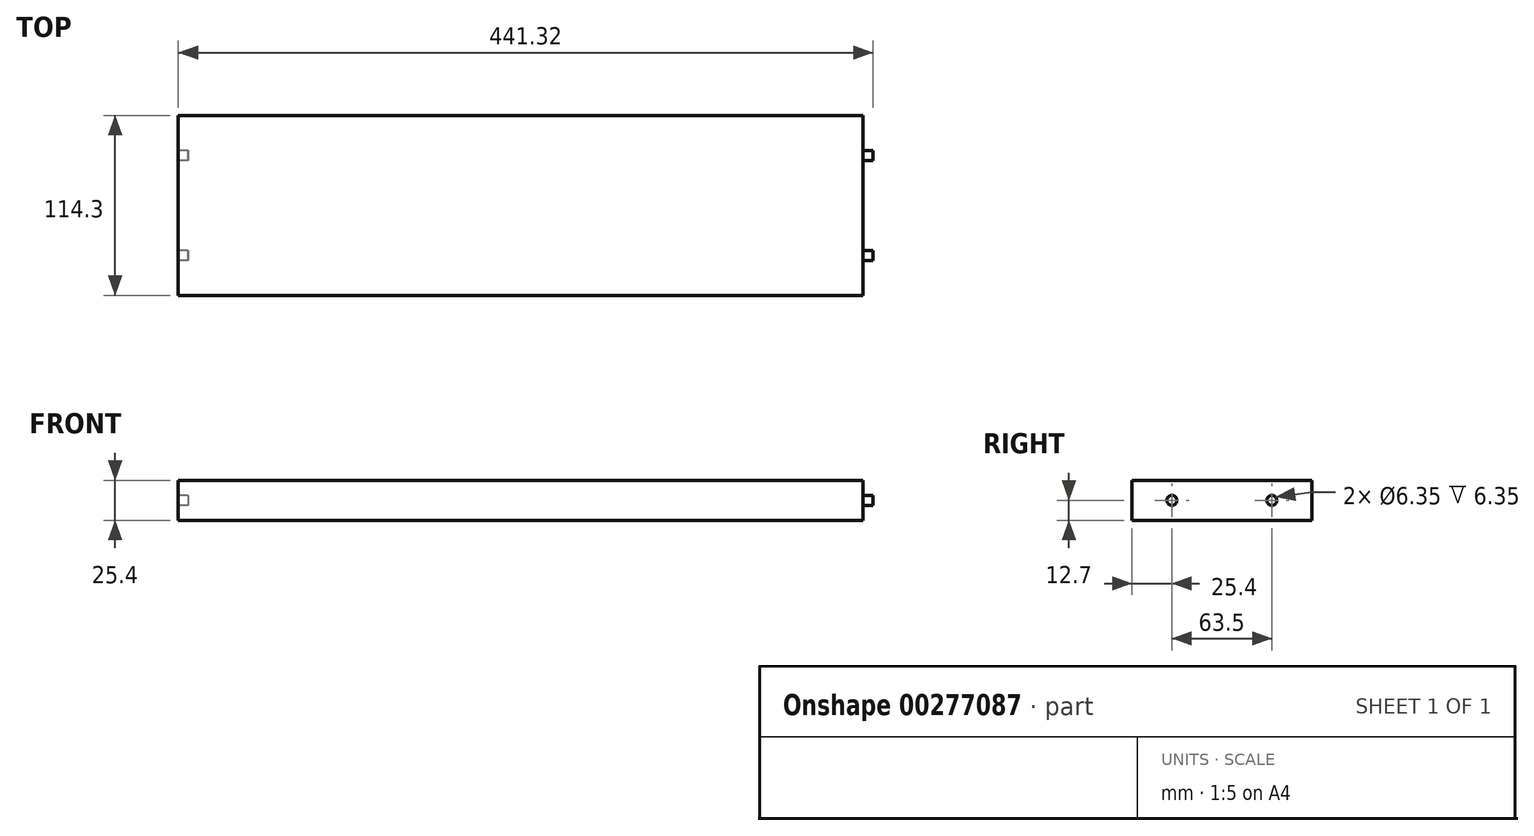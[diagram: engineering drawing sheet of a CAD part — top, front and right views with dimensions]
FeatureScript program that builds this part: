
annotation { "Feature Type Name" : "Feature", "Feature Type Description" : "" }
export const myFeature = defineFeature(function(context is Context, id is Id, definition is map)
    precondition{}
    {
        {
            var Q0;
            Q0=qCreatedBy(makeId("Front.planeOp"),FACE);
            var sketch = newSketch(context, id + "F0", { "sketchPlane" : qUnion([Q0])});
            skLineSegment(sketch, "E0.bottom", {"start": v(-71.67, 0) * mm, "end": v(369.65, 0) * mm});
            skLineSegment(sketch, "E0.top", {"start": v(-71.67, 25.4) * mm, "end": v(369.65, 25.4) * mm});
            skLineSegment(sketch, "E0.left", {"start": v(-71.67, 0) * mm, "end": v(-71.67, 25.4) * mm});
            skLineSegment(sketch, "E0.right", {"start": v(369.65, 0) * mm, "end": v(369.65, 25.4) * mm});
            skSolve(sketch);
        }
        {
            var Q0;
            Q0=makeQuery(id+"F0.imprint","IMPRINT",FACE,{"disambiguationData":[TD([[makeQuery(id+"F0.imprint","IMPRINT",EDGE,{"derivedFrom":sQuery(id+"F0.wireOp",EDGE,"E0.bottom")}),1.0]])]});
            extrude(context, id + "F1", {"entities" : qUnion([Q0]), "depth" : 114.3 * mm});
        }
        {
            var Q0;
            Q0=makeQuery(id+"F1.opExtrude","SWEPT_FACE",FACE,{"disambiguationData":[OSD([sQuery(id+"F0.wireOp",EDGE,"E0.left")])]});
            var sketch = newSketch(context, id + "F2", { "sketchPlane" : qUnion([Q0])});
            skCircle(sketch, "E1", {"center": v(25.4, 12.7) * mm, "radius": 3.18 * mm});
            skPoint(sketch, "E1.centerSnap0", {"position": v(0, 12.7) * mm});
            skCircle(sketch, "E2", {"center": v(88.9, 12.7) * mm, "radius": 3.18 * mm});
            skPoint(sketch, "E2.centerSnap0", {"position": v(114.3, 12.7) * mm});
            skSolve(sketch);
        }
        {
            var Q0;
            Q0=makeQuery(id+"F1.opExtrude","SWEPT_FACE",FACE,{"disambiguationData":[OSD([sQuery(id+"F0.wireOp",EDGE,"E0.right")])]});
            var sketch = newSketch(context, id + "F3", { "sketchPlane" : qUnion([Q0])});
            skCircle(sketch, "E3.0", {"center": v(-88.9, 12.7) * mm, "radius": 3.18 * mm});
            skCircle(sketch, "E4.0", {"center": v(-25.4, 12.7) * mm, "radius": 3.18 * mm});
            skSolve(sketch);
        }
        {
            var Q0;
            Q0=makeQuery(id+"F3.imprint","IMPRINT",FACE,{"disambiguationData":[TD([[makeQuery(id+"F3.imprint","IMPRINT",EDGE,{"derivedFrom":sQuery(id+"F3.wireOp",EDGE,"E3.0")}),-1.0]])]});
            var Q1;
            Q1=makeQuery(id+"F3.imprint","IMPRINT",FACE,{"disambiguationData":[TD([[makeQuery(id+"F3.imprint","IMPRINT",EDGE,{"derivedFrom":sQuery(id+"F3.wireOp",EDGE,"E4.0")}),-1.0]])]});
            extrude(context, id + "F4", {"entities" : qUnion([Q0, Q1]), "operationType" : NewBodyOperationType.REMOVE, "oppositeDirection" : true, "depth" : 6.35 * mm});
        }
        {
            var Q0;
            Q0=makeQuery(id+"F2.imprint","IMPRINT",FACE,{"disambiguationData":[TD([[makeQuery(id+"F2.imprint","IMPRINT",EDGE,{"derivedFrom":sQuery(id+"F2.wireOp",EDGE,"E1")}),1.0]])]});
            var Q1;
            Q1=makeQuery(id+"F2.imprint","IMPRINT",FACE,{"disambiguationData":[TD([[makeQuery(id+"F2.imprint","IMPRINT",EDGE,{"derivedFrom":sQuery(id+"F2.wireOp",EDGE,"E2")}),1.0]])]});
            extrude(context, id + "F5", {"entities" : qUnion([Q0, Q1]), "operationType" : NewBodyOperationType.REMOVE, "oppositeDirection" : true, "depth" : 6.35 * mm});
        }
    });
